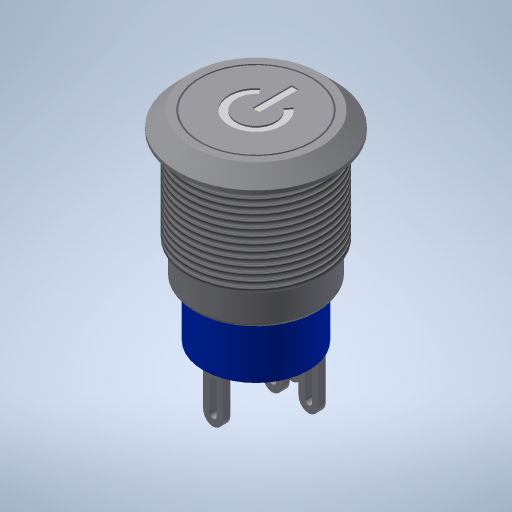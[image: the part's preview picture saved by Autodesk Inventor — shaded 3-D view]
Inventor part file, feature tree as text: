
AUTODESK INVENTOR PART (.ipt)
format: ipt  version: 2024 (Build 280153000, 153)  size: 444,416 bytes
history: native  units: mm
features: sketch x16, extrude x13, fillet x2, chamfer x1, thread x1
ambient origin geometry x8: Origin, YZ Plane, XZ Plane, XY Plane, X Axis, Y Axis, Z Axis, Center Point
bodies: Solido1 (feature_tree)
feature tree (33):
  extrude  "Estrusione1"  Depth=13.0mm TaperAngle=0.0deg
  extrude  "Estrusione2"  Depth=0.8mm TaperAngle=0.0deg
  extrude  "Estrusione3"  Depth=1.7mm TaperAngle=0.0deg
  chamfer  "Smusso1"  Distance=2.0mm Angle=45.0deg
  sketch  "Schizzo4"
  extrude  "Estrusione4"  Depth=4.8mm TaperAngle=0.0deg
  fillet  "Raccordo1"  Radius=0.5mm
  extrude  "Estrusione5"  Depth=7.6mm TaperAngle=0.0deg
  thread  "Filettatura1"
  sketch  "Schizzo7"
  extrude  "Estrusione6"  Depth=10.0mm TaperAngle=0.0deg
  extrude  "Estrusione7"  Depth=2.0mm TaperAngle=0.0deg
  sketch  "Schizzo10"
  sketch  "Schizzo11"
  extrude  "Estrusione8"  Depth=0.2mm TaperAngle=0.0deg
  fillet  "Raccordo2"  Radius=7.5mm
  extrude  "Estrusione9"  Depth=1.5mm
  extrude  "Estrusione10"  Depth=1.0mm TaperAngle=0.0deg
  extrude  "Estrusione11"  Depth=1.0mm TaperAngle=0.0deg
  extrude  "Estrusione12"  Depth=1.0mm TaperAngle=0.0deg
  extrude  "Estrusione13"  Depth=1.0mm TaperAngle=0.0deg
  sketch  "Schizzo1"
  sketch  "Schizzo2"
  sketch  "Schizzo3"
  sketch  "Schizzo5"
  sketch  "Schizzo6"
  sketch  "Schizzo8"
  sketch  "Schizzo9"
  sketch  "Schizzo12"
  sketch  "Schizzo13"
  sketch  "Schizzo14"
  sketch  "Schizzo15"
  sketch  "Schizzo16"
